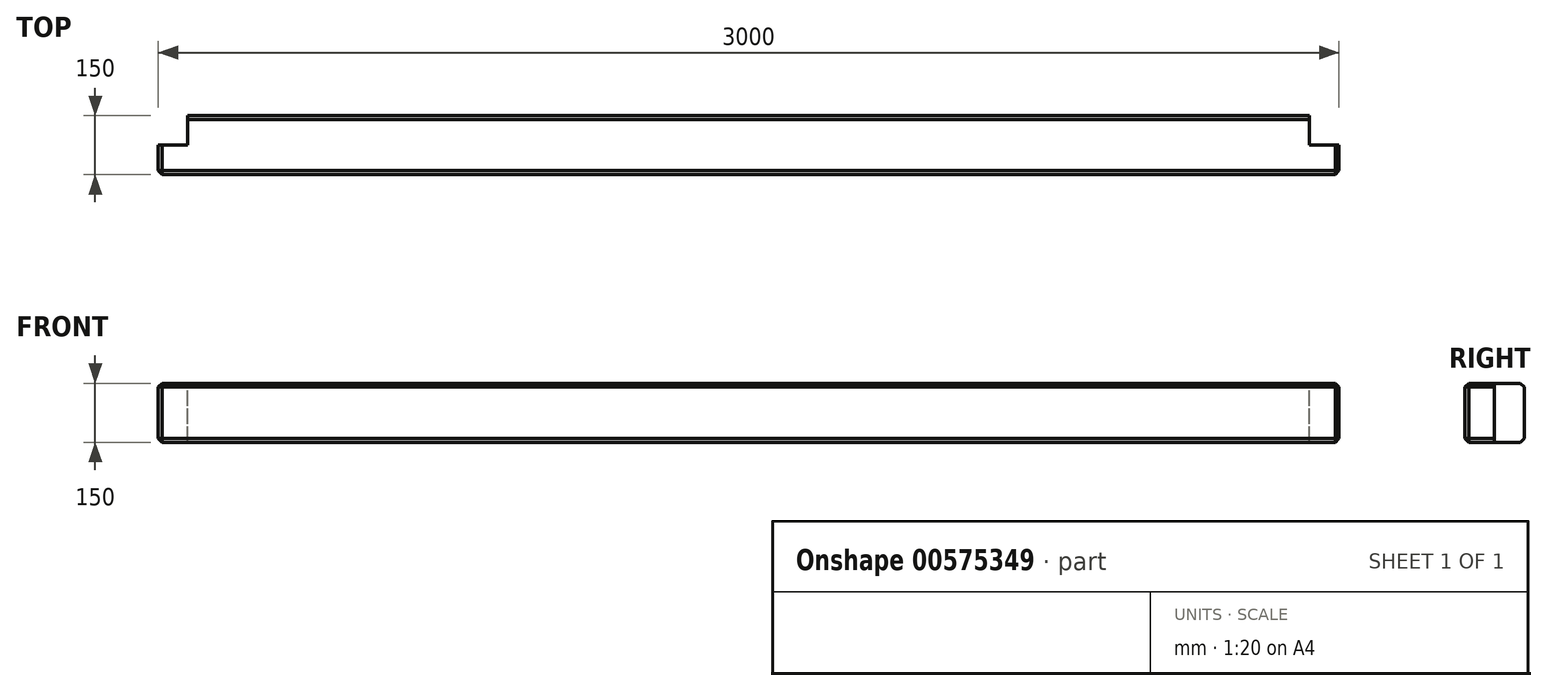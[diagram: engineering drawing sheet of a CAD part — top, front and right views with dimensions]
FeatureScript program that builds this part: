
annotation { "Feature Type Name" : "Feature", "Feature Type Description" : "" }
export const myFeature = defineFeature(function(context is Context, id is Id, definition is map)
    precondition{}
    {
        {
            var Q0;
            Q0=qCreatedBy(makeId("Top.planeOp"),FACE);
            var sketch = newSketch(context, id + "F0", { "sketchPlane" : qUnion([Q0])});
            skLineSegment(sketch, "E0.bottom", {"start": v(-1500, 75) * mm, "end": v(1500, 75) * mm});
            skLineSegment(sketch, "E0.top", {"start": v(-1500, -75) * mm, "end": v(1500, -75) * mm});
            skLineSegment(sketch, "E0.left", {"start": v(-1500, 75) * mm, "end": v(-1500, -75) * mm});
            skLineSegment(sketch, "E0.right", {"start": v(1500, 75) * mm, "end": v(1500, -75) * mm});
            skPoint(sketch, "E0.middle", {"position": v(0, 0) * mm});
            skSolve(sketch);
        }
        {
            var Q0;
            Q0=makeQuery(id+"F0.imprint","IMPRINT",FACE,{"disambiguationData":[TD([[makeQuery(id+"F0.imprint","IMPRINT",EDGE,{"derivedFrom":sQuery(id+"F0.wireOp",EDGE,"E0.bottom")}),-1.0]])]});
            extrude(context, id + "F1", {"entities" : qUnion([Q0]), "depth" : 150 * mm});
        }
        {
            var Q0;
            Q0=makeQuery(id+"F1.opExtrude","SWEPT_FACE",FACE,{"disambiguationData":[OSD([sQuery(id+"F0.wireOp",EDGE,"E0.top")])]});
            var Q1;
            Q1=makeQuery(id+"F1.opExtrude","CAP_FACE",FACE,{"disambiguationData":[OSD([sQuery(id+"F0.wireOp",EDGE,"E0.bottom"),sQuery(id+"F0.wireOp",EDGE,"E0.top"),sQuery(id+"F0.wireOp",EDGE,"E0.left"),sQuery(id+"F0.wireOp",EDGE,"E0.right")])],"isStart":false});
            var Q2;
            Q2=makeQuery(id+"F1.opExtrude","SWEPT_FACE",FACE,{"disambiguationData":[OSD([sQuery(id+"F0.wireOp",EDGE,"E0.left")])]});
            var Q3;
            Q3=makeQuery(id+"F1.opExtrude","CAP_FACE",FACE,{"disambiguationData":[OSD([sQuery(id+"F0.wireOp",EDGE,"E0.bottom"),sQuery(id+"F0.wireOp",EDGE,"E0.top"),sQuery(id+"F0.wireOp",EDGE,"E0.left"),sQuery(id+"F0.wireOp",EDGE,"E0.right")])],"isStart":true});
            var Q4;
            Q4=makeQuery(id+"F1.opExtrude","SWEPT_FACE",FACE,{"disambiguationData":[OSD([sQuery(id+"F0.wireOp",EDGE,"E0.bottom")])]});
            var Q5;
            Q5=makeQuery(id+"F1.opExtrude","SWEPT_FACE",FACE,{"disambiguationData":[OSD([sQuery(id+"F0.wireOp",EDGE,"E0.right")])]});
            chamfer(context, id + "F2", {"entities" : qUnion([Q0, Q1, Q2, Q3, Q4, Q5]), "width" : 10 * mm, "tangentPropagation" : true});
        }
        {
            var Q0;
            Q0=makeQuery(id+"F1.opExtrude","CAP_FACE",FACE,{"disambiguationData":[OSD([sQuery(id+"F0.wireOp",EDGE,"E0.bottom"),sQuery(id+"F0.wireOp",EDGE,"E0.top"),sQuery(id+"F0.wireOp",EDGE,"E0.left"),sQuery(id+"F0.wireOp",EDGE,"E0.right")])],"isStart":false});
            var sketch = newSketch(context, id + "F3", { "sketchPlane" : qUnion([Q0])});
            skPoint(sketch, "E1", {"position": v(-1425, 75) * mm});
            skPoint(sketch, "E2.oppositeSnap0", {"position": v(-1490, 0) * mm});
            skLineSegment(sketch, "E2.bottom", {"start": v(-1425, 75) * mm, "end": v(-1500, 75) * mm});
            skLineSegment(sketch, "E2.top", {"start": v(-1425, 0) * mm, "end": v(-1500, 0) * mm});
            skLineSegment(sketch, "E2.left", {"start": v(-1425, 75) * mm, "end": v(-1425, 0) * mm});
            skLineSegment(sketch, "E2.right", {"start": v(-1500, 75) * mm, "end": v(-1500, 0) * mm});
            skSolve(sketch);
        }
        {
            var Q0;
            {var subQ0=sQuery(id+"F3.wireOp",EDGE,"E2.left");var subQ1=sQuery(id+"F3.wireOp",EDGE,"E2.top");var subQ2=makeQuery(id+"F3.imprint","INTERSECT",VERTEX,{"derivedFrom":[subQ1,subQ0]});Q0=makeQuery(id+"F3.imprint","IMPRINT",FACE,{"disambiguationData":[TD([[makeQuery(id+"F3.imprint","IMPRINT",EDGE,{"disambiguationData":[TD([[subQ2,-1.0]])],"derivedFrom":subQ1}),-1.0]])]});}
            var Q1;
            {var subQ1=sQuery(id+"F3.wireOp",EDGE,"E2.bottom");Q1=makeQuery(id+"F3.imprint","IMPRINT",FACE,{"disambiguationData":[TD([[makeQuery(id+"F3.imprint","IMPRINT",EDGE,{"derivedFrom":subQ1}),1.0]])]});}
            extrude(context, id + "F4", {"entities" : qUnion([Q0, Q1]), "operationType" : NewBodyOperationType.REMOVE, "endBound" : BoundingType.THROUGH_ALL, "oppositeDirection" : true, "depth" : 25 * mm});
        }
        {
            var Q0;
            Q0=makeQuery(id+"F1.opExtrude","CAP_FACE",FACE,{"disambiguationData":[OSD([sQuery(id+"F0.wireOp",EDGE,"E0.bottom"),sQuery(id+"F0.wireOp",EDGE,"E0.top"),sQuery(id+"F0.wireOp",EDGE,"E0.left"),sQuery(id+"F0.wireOp",EDGE,"E0.right")])],"isStart":false});
            var sketch = newSketch(context, id + "F5", { "sketchPlane" : qUnion([Q0])});
            skPoint(sketch, "E3", {"position": v(1425, 75) * mm});
            skPoint(sketch, "E4.oppositeSnap0", {"position": v(1490, 0) * mm});
            skLineSegment(sketch, "E4.bottom", {"start": v(1425, 75) * mm, "end": v(1500, 75) * mm});
            skLineSegment(sketch, "E4.top", {"start": v(1425, 0) * mm, "end": v(1500, 0) * mm});
            skLineSegment(sketch, "E4.left", {"start": v(1425, 75) * mm, "end": v(1425, 0) * mm});
            skLineSegment(sketch, "E4.right", {"start": v(1500, 75) * mm, "end": v(1500, 0) * mm});
            skSolve(sketch);
        }
        {
            var Q0;
            {var subQ2=sQuery(id+"F5.wireOp",EDGE,"E4.bottom");Q0=makeQuery(id+"F5.imprint","IMPRINT",FACE,{"disambiguationData":[TD([[makeQuery(id+"F5.imprint","IMPRINT",EDGE,{"derivedFrom":subQ2}),-1.0]])]});}
            var Q1;
            {var subQ0=sQuery(id+"F5.wireOp",EDGE,"E4.left");var subQ1=sQuery(id+"F5.wireOp",EDGE,"E4.top");var subQ2=makeQuery(id+"F5.imprint","INTERSECT",VERTEX,{"derivedFrom":[subQ1,subQ0]});Q1=makeQuery(id+"F5.imprint","IMPRINT",FACE,{"disambiguationData":[TD([[makeQuery(id+"F5.imprint","IMPRINT",EDGE,{"disambiguationData":[TD([[subQ2,-1.0]])],"derivedFrom":subQ1}),1.0]])]});}
            extrude(context, id + "F6", {"entities" : qUnion([Q0, Q1]), "operationType" : NewBodyOperationType.REMOVE, "endBound" : BoundingType.THROUGH_ALL, "oppositeDirection" : true, "depth" : 25 * mm});
        }
    });
